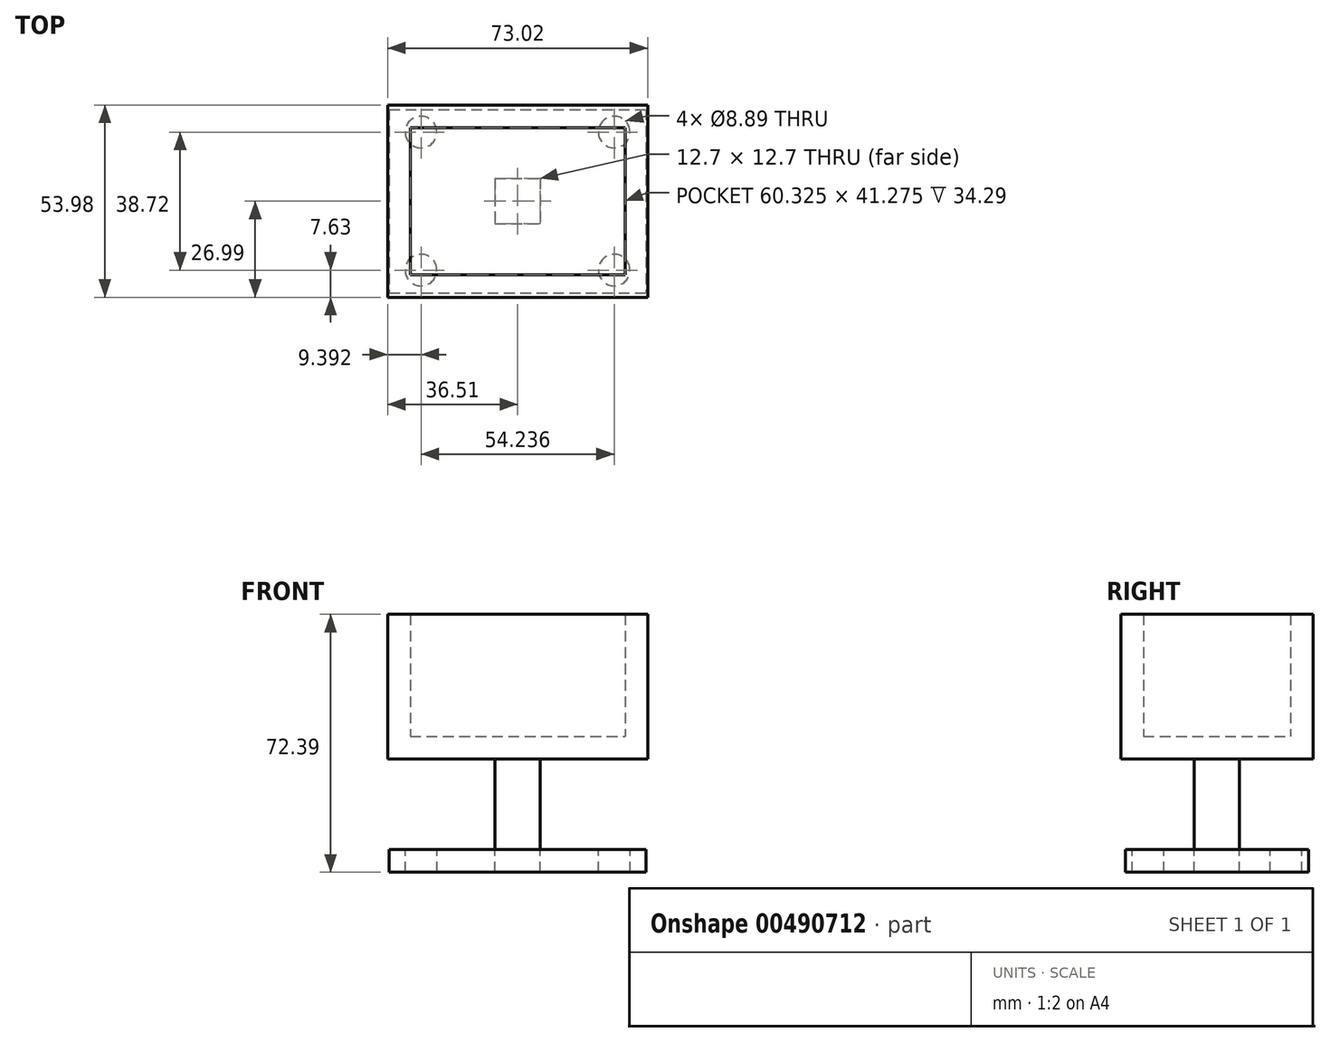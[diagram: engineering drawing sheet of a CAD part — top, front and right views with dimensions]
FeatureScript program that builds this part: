
annotation { "Feature Type Name" : "Feature", "Feature Type Description" : "" }
export const myFeature = defineFeature(function(context is Context, id is Id, definition is map)
    precondition{}
    {
        {
            var Q0;
            Q0=qCreatedBy(makeId("Top.planeOp"),FACE);
            var sketch = newSketch(context, id + "F0", { "sketchPlane" : qUnion([Q0])});
            skLineSegment(sketch, "E0.bottom", {"start": v(-30.16, -20.64) * mm, "end": v(30.16, -20.64) * mm});
            skLineSegment(sketch, "E0.top", {"start": v(-30.16, 20.64) * mm, "end": v(30.16, 20.64) * mm});
            skLineSegment(sketch, "E0.left", {"start": v(-30.16, -20.64) * mm, "end": v(-30.16, 20.64) * mm});
            skLineSegment(sketch, "E0.right", {"start": v(30.16, -20.64) * mm, "end": v(30.16, 20.64) * mm});
            skPoint(sketch, "E0.middle", {"position": v(0, 0) * mm});
            skSolve(sketch);
        }
        {
            var Q0;
            Q0=makeQuery(id+"F0.imprint","IMPRINT",FACE,{"disambiguationData":[TD([[makeQuery(id+"F0.imprint","IMPRINT",EDGE,{"derivedFrom":sQuery(id+"F0.wireOp",EDGE,"E0.bottom")}),1.0]])]});
            extrude(context, id + "F1", {"entities" : qUnion([Q0]), "depth" : 6.35 * mm});
        }
        {
            var Q0;
            Q0=makeQuery(id+"F1.opExtrude","CAP_FACE",FACE,{"disambiguationData":[OSD([sQuery(id+"F0.wireOp",EDGE,"E0.bottom"),sQuery(id+"F0.wireOp",EDGE,"E0.top"),sQuery(id+"F0.wireOp",EDGE,"E0.left"),sQuery(id+"F0.wireOp",EDGE,"E0.right")])],"isStart":true});
            var sketch = newSketch(context, id + "F2", { "sketchPlane" : qUnion([Q0])});
            skLineSegment(sketch, "E1.bottom", {"start": v(-6.35, -6.35) * mm, "end": v(6.35, -6.35) * mm});
            skLineSegment(sketch, "E1.top", {"start": v(-6.35, 6.35) * mm, "end": v(6.35, 6.35) * mm});
            skLineSegment(sketch, "E1.left", {"start": v(-6.35, -6.35) * mm, "end": v(-6.35, 6.35) * mm});
            skLineSegment(sketch, "E1.right", {"start": v(6.35, -6.35) * mm, "end": v(6.35, 6.35) * mm});
            skPoint(sketch, "E1.middle", {"position": v(0, 0) * mm});
            skSolve(sketch);
        }
        {
            var Q0;
            Q0=makeQuery(id+"F2.imprint","IMPRINT",FACE,{"disambiguationData":[TD([[makeQuery(id+"F2.imprint","IMPRINT",EDGE,{"derivedFrom":sQuery(id+"F2.wireOp",EDGE,"E1.bottom")}),1.0]])]});
            extrude(context, id + "F3", {"entities" : qUnion([Q0]), "operationType" : NewBodyOperationType.ADD, "depth" : 25.4 * mm});
        }
        {
            var Q0;
            Q0=makeQuery(id+"F3.opExtrude","CAP_FACE",FACE,{"disambiguationData":[OSD([sQuery(id+"F2.wireOp",EDGE,"E1.bottom"),sQuery(id+"F2.wireOp",EDGE,"E1.top"),sQuery(id+"F2.wireOp",EDGE,"E1.left"),sQuery(id+"F2.wireOp",EDGE,"E1.right")])],"isStart":false});
            var sketch = newSketch(context, id + "F4", { "sketchPlane" : qUnion([Q0])});
            skLineSegment(sketch, "E2.bottom", {"start": v(-36, -25.7) * mm, "end": v(36, -25.7) * mm});
            skLineSegment(sketch, "E2.top", {"start": v(-36, 25.7) * mm, "end": v(36, 25.7) * mm});
            skLineSegment(sketch, "E2.left", {"start": v(-36, -25.7) * mm, "end": v(-36, 25.7) * mm});
            skLineSegment(sketch, "E2.right", {"start": v(36, -25.7) * mm, "end": v(36, 25.7) * mm});
            skPoint(sketch, "E2.middle", {"position": v(0, 0) * mm});
            skLineSegment(sketch, "E3", {"start": v(-36, 25.7) * mm, "end": v(0, 0) * mm});
            skLineSegment(sketch, "E4", {"start": v(0, 0) * mm, "end": v(-36, -25.7) * mm});
            skLineSegment(sketch, "E5", {"start": v(0, 0) * mm, "end": v(36, 25.7) * mm});
            skLineSegment(sketch, "E6", {"start": v(0, 0) * mm, "end": v(36, -25.7) * mm});
            skCircle(sketch, "E7", {"center": v(-27.12, 19.36) * mm, "radius": 4.45 * mm});
            skCircle(sketch, "E8", {"center": v(-27.12, -19.36) * mm, "radius": 4.45 * mm});
            skCircle(sketch, "E9", {"center": v(27.12, -19.36) * mm, "radius": 4.45 * mm});
            skCircle(sketch, "E10", {"center": v(27.12, 19.36) * mm, "radius": 4.45 * mm});
            skSolve(sketch);
        }
        {
            var Q0;
            {var subQ10=sQuery(id+"F4.wireOp",EDGE,"E2.left");Q0=makeQuery(id+"F4.imprint","IMPRINT",FACE,{"disambiguationData":[TD([[makeQuery(id+"F4.imprint","IMPRINT",EDGE,{"derivedFrom":subQ10}),-1.0]])]});}
            var Q1;
            {var subQ6=sQuery(id+"F4.wireOp",EDGE,"E2.top");Q1=makeQuery(id+"F4.imprint","IMPRINT",FACE,{"disambiguationData":[TD([[makeQuery(id+"F4.imprint","IMPRINT",EDGE,{"derivedFrom":subQ6}),-1.0]])]});}
            var Q2;
            {var subQ6=sQuery(id+"F4.wireOp",EDGE,"E2.right");Q2=makeQuery(id+"F4.imprint","IMPRINT",FACE,{"disambiguationData":[TD([[makeQuery(id+"F4.imprint","IMPRINT",EDGE,{"derivedFrom":subQ6}),1.0]])]});}
            var Q3;
            {var subQ7=sQuery(id+"F4.wireOp",EDGE,"E2.bottom");Q3=makeQuery(id+"F4.imprint","IMPRINT",FACE,{"disambiguationData":[TD([[makeQuery(id+"F4.imprint","IMPRINT",EDGE,{"derivedFrom":subQ7}),1.0]])]});}
            extrude(context, id + "F5", {"entities" : qUnion([Q0, Q1, Q2, Q3]), "depth" : 6.35 * mm});
        }
        {
            var Q0;
            Q0=makeQuery(id+"F1.opExtrude","CAP_FACE",FACE,{"disambiguationData":[OSD([sQuery(id+"F0.wireOp",EDGE,"E0.bottom"),sQuery(id+"F0.wireOp",EDGE,"E0.top"),sQuery(id+"F0.wireOp",EDGE,"E0.left"),sQuery(id+"F0.wireOp",EDGE,"E0.right")])],"isStart":true});
            var sketch = newSketch(context, id + "F6", { "sketchPlane" : qUnion([Q0])});
            skLineSegment(sketch, "E11.bottom", {"start": v(-30.16, 20.64) * mm, "end": v(-30.16, 20.64) * mm});
            skLineSegment(sketch, "E11.top", {"start": v(-30.16, -20.64) * mm, "end": v(-30.16, -20.64) * mm});
            skLineSegment(sketch, "E11.left", {"start": v(-30.16, 20.64) * mm, "end": v(-30.16, -20.64) * mm});
            skLineSegment(sketch, "E11.right", {"start": v(-30.16, 20.64) * mm, "end": v(-30.16, -20.64) * mm});
            skLineSegment(sketch, "E12", {"start": v(-36.51, -20.64) * mm, "end": v(-36.51, 20.64) * mm});
            skLineSegment(sketch, "E13", {"start": v(-36.51, 20.64) * mm, "end": v(-30.16, 20.64) * mm});
            skLineSegment(sketch, "E14", {"start": v(30.16, 20.64) * mm, "end": v(30.16, -20.64) * mm});
            skLineSegment(sketch, "E15", {"start": v(30.16, -20.64) * mm, "end": v(36.51, -20.64) * mm});
            skLineSegment(sketch, "E16", {"start": v(36.51, -20.64) * mm, "end": v(36.51, 20.64) * mm});
            skLineSegment(sketch, "E17", {"start": v(36.51, 20.64) * mm, "end": v(30.16, 20.64) * mm});
            skLineSegment(sketch, "E18.bottom", {"start": v(36.51, -20.64) * mm, "end": v(-36.51, -20.64) * mm});
            skLineSegment(sketch, "E18.top", {"start": v(36.51, -26.99) * mm, "end": v(-36.51, -26.99) * mm});
            skLineSegment(sketch, "E18.left", {"start": v(36.51, -20.64) * mm, "end": v(36.51, -26.99) * mm});
            skLineSegment(sketch, "E18.right", {"start": v(-36.51, -20.64) * mm, "end": v(-36.51, -26.99) * mm});
            skLineSegment(sketch, "E19.bottom", {"start": v(36.51, 20.64) * mm, "end": v(-36.51, 20.64) * mm});
            skLineSegment(sketch, "E19.top", {"start": v(36.51, 26.99) * mm, "end": v(-36.51, 26.99) * mm});
            skLineSegment(sketch, "E19.left", {"start": v(36.51, 20.64) * mm, "end": v(36.51, 26.99) * mm});
            skLineSegment(sketch, "E19.right", {"start": v(-36.51, 20.64) * mm, "end": v(-36.51, 26.99) * mm});
            skSolve(sketch);
        }
        {
            var Q0;
            Q0 = qSketchRegion(id + "F6", true);
            extrude(context, id + "F7", {"entities" : qUnion([Q0]), "operationType" : NewBodyOperationType.ADD, "oppositeDirection" : true, "depth" : 40.64 * mm});
        }
    });
